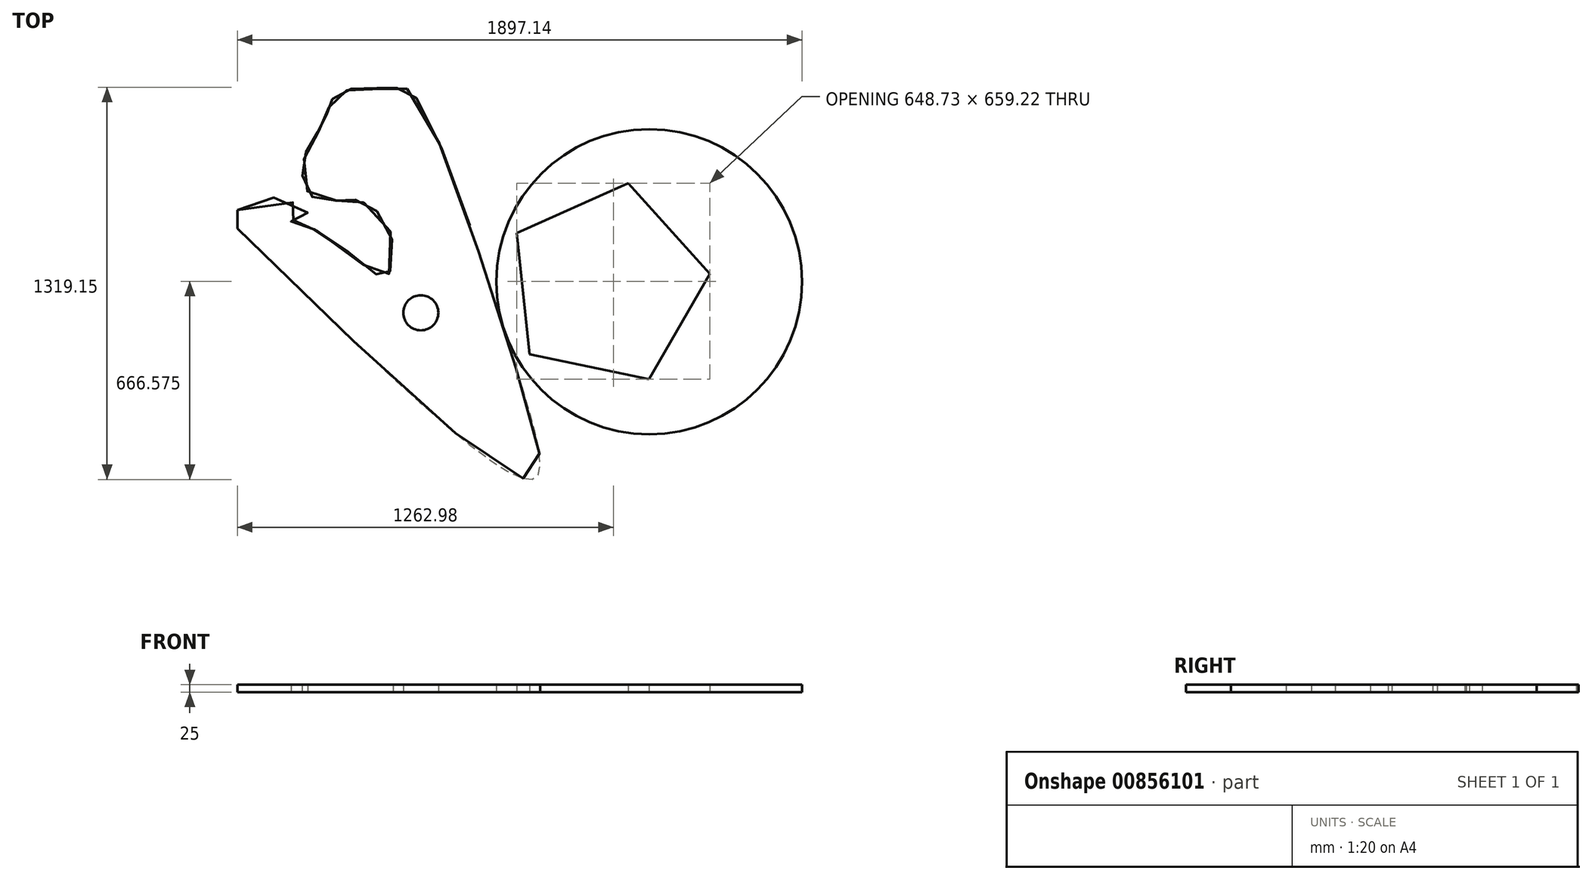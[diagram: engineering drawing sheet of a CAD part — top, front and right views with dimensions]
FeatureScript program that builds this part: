
annotation { "Feature Type Name" : "Feature", "Feature Type Description" : "" }
export const myFeature = defineFeature(function(context is Context, id is Id, definition is map)
    precondition{}
    {
        {
            var Q0;
            Q0=qCreatedBy(makeId("Top.planeOp"),FACE);
            var sketch = newSketch(context, id + "F0", { "sketchPlane" : qUnion([Q0])});
            skFitSpline(sketch, "E0", {"points": [v(0, 0) * mm, v(992.4, -842.97) * mm, v(918.12, -413.31) * mm, v(575.88, 466.87) * mm, v(517.33, 469.06) * mm, v(431.63, 474.97) * mm, v(330.42, 447.4) * mm, v(307.26, 406.93) * mm, v(288.21, 354.25) * mm, v(242.23, 281.19) * mm, v(217.68, 189.8) * mm, v(254.6, 104.3) * mm, v(350.85, 96.01) * mm, v(412.27, 92.04) * mm, v(509.97, 0) * mm, v(505.66, -157) * mm, v(463.5, -152.26) * mm, v(250.37, 0) * mm, v(181.42, 25.52) * mm, v(235.57, 58.14) * mm, v(0, 62.74) * mm], "startDerivative": vector(8961.43, -8776.18) * mm, "endDerivative": vector(0, -4329.85) * mm});
            skLineSegment(sketch, "E1", {"start": v(0, 62.74) * mm, "end": v(0, 0) * mm});
            skCircle(sketch, "E2", {"center": v(616.24, -283.37) * mm, "radius": 58.83 * mm});
            skCircle(sketch, "E3", {"center": v(1383.7, -178.83) * mm, "radius": 513.43 * mm});
            skCircle(sketch, "E4.cCircle", {"center": v(1240.77, -189.05) * mm, "radius": 281.98 * mm, "construction": true});
            skLineSegment(sketch, "E4.0", {"start": v(1312.63, 152) * mm, "end": v(1587.35, -152) * mm});
            skLineSegment(sketch, "E4.1", {"start": v(1587.35, -152) * mm, "end": v(1383.1, -507.22) * mm});
            skLineSegment(sketch, "E4.2", {"start": v(1383.1, -507.22) * mm, "end": v(982.17, -422.74) * mm});
            skLineSegment(sketch, "E4.3", {"start": v(982.17, -422.74) * mm, "end": v(938.61, -15.32) * mm});
            skLineSegment(sketch, "E4.4", {"start": v(938.61, -15.32) * mm, "end": v(1312.63, 152) * mm});
            skPoint(sketch, "E4.0.midPoint", {"position": v(1450, 0) * mm});
            skSolve(sketch);
        }
        {
            var Q0;
            Q0 = qSketchRegion(id + "F0", true);
            extrude(context, id + "F1", {"entities" : qUnion([Q0]), "depth" : 25 * mm, "offsetDistance" : 25 * mm});
        }
    });
